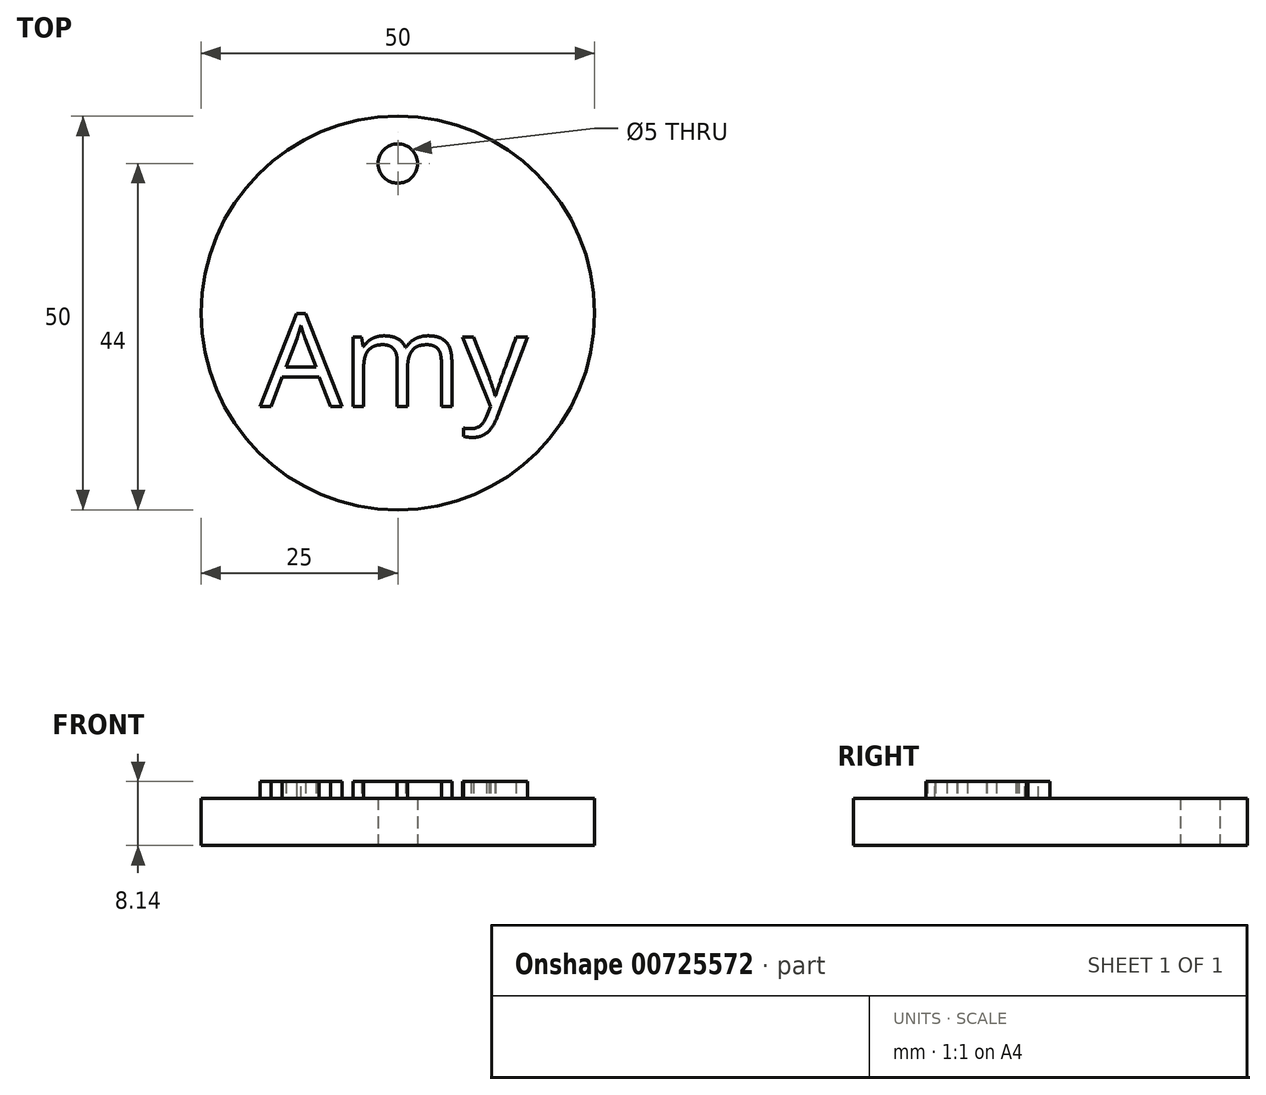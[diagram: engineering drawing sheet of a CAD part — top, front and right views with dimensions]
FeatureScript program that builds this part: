
annotation { "Feature Type Name" : "Feature", "Feature Type Description" : "" }
export const myFeature = defineFeature(function(context is Context, id is Id, definition is map)
    precondition{}
    {
        {
            var Q0;
            Q0=qCreatedBy(makeId("Top.planeOp"),FACE);
            var sketch = newSketch(context, id + "F0", { "sketchPlane" : qUnion([Q0])});
            skCircle(sketch, "E0", {"center": v(0, 0) * mm, "radius": 25 * mm});
            skLineSegment(sketch, "E1", {"start": v(0, 0) * mm, "end": v(0, 25) * mm, "construction": true});
            skCircle(sketch, "E2", {"center": v(0, 19) * mm, "radius": 2.5 * mm});
            skSolve(sketch);
        }
        {
            var Q0;
            Q0=makeQuery(id+"F0.imprint","IMPRINT",FACE,{"disambiguationData":[TD([[makeQuery(id+"F0.imprint","IMPRINT",EDGE,{"derivedFrom":sQuery(id+"F0.wireOp",EDGE,"E0")}),1.0]])]});
            extrude(context, id + "F1", {"entities" : qUnion([Q0]), "depth" : 6 * mm, "offsetDistance" : 25 * mm});
        }
        {
            var Q0;
            Q0=makeQuery(id+"F1.opExtrude","CAP_FACE",FACE,{"disambiguationData":[OSD([sQuery(id+"F0.wireOp",EDGE,"E0"),sQuery(id+"F0.wireOp",EDGE,"E2")])],"isStart":false});
            var sketch = newSketch(context, id + "F2", { "sketchPlane" : qUnion([Q0])});
            skLineSegment(sketch, "E3", {"start": v(0, 0) * mm, "end": v(0, 19) * mm, "construction": true});
            skText(sketch, "E4", { "text": "Amy", "fontName": "OpenSans-Regular.ttf"});
            const initialGuessF2  = {"E4": [-0.01751, -0.01184, 1, 0, 0.01184]};
            skSetInitialGuess(sketch, initialGuessF2);
            skSolve(sketch);
        }
        {
            var Q0;
            Q0 = qSketchRegion(id + "F2", true);
            extrude(context, id + "F3", {"entities" : qUnion([Q0]), "operationType" : NewBodyOperationType.ADD, "depth" : 2.14 * mm, "offsetDistance" : 25 * mm});
        }
    });
